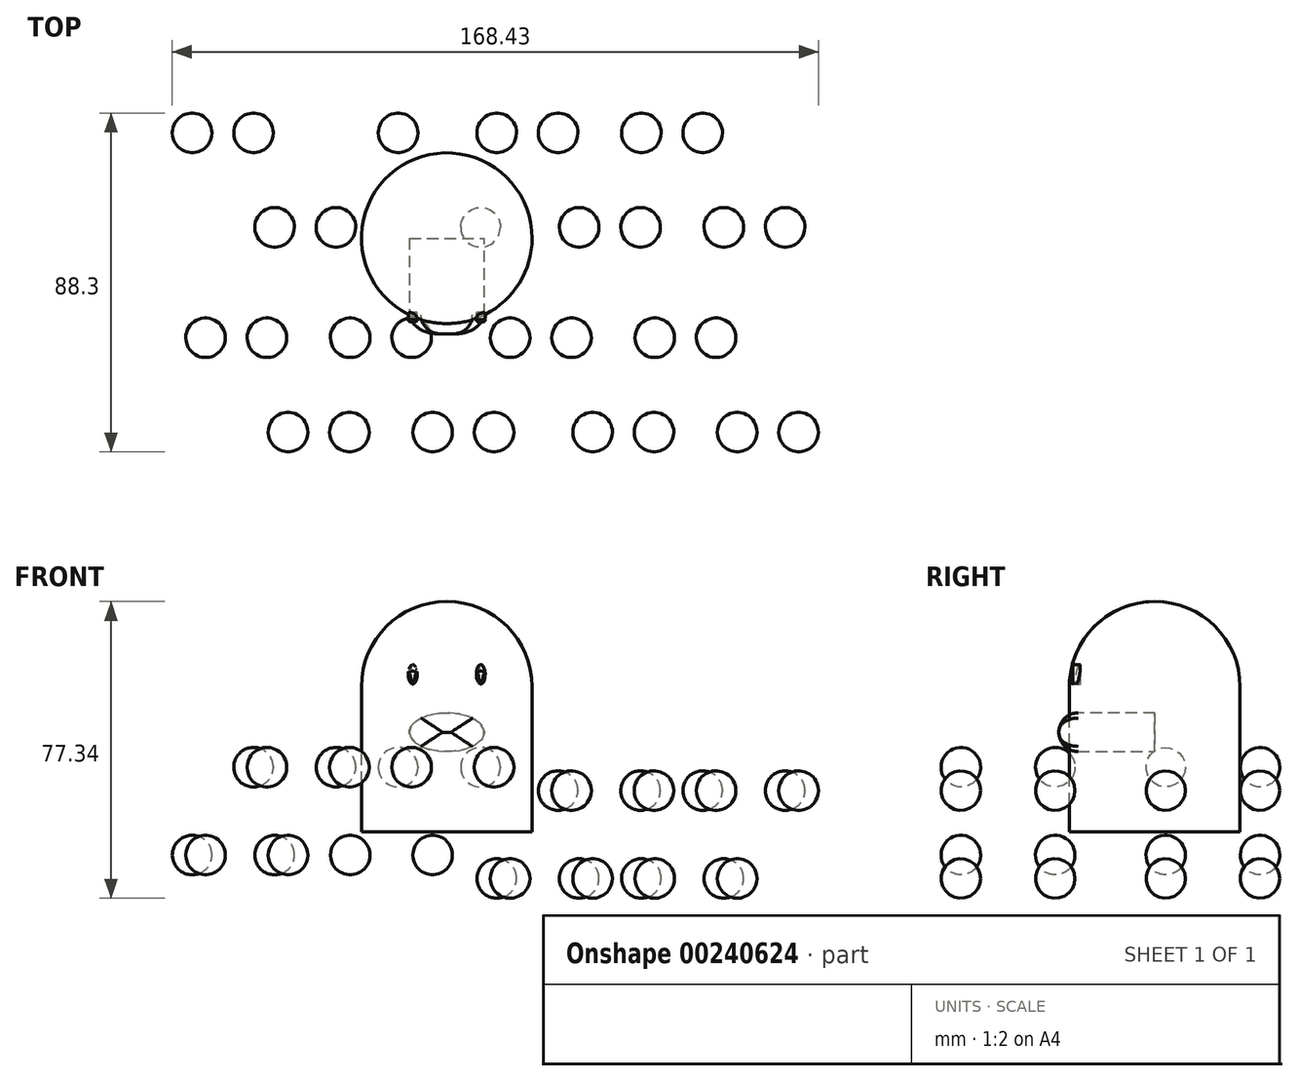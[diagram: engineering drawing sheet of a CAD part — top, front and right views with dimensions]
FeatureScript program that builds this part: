
annotation { "Feature Type Name" : "Feature", "Feature Type Description" : "" }
export const myFeature = defineFeature(function(context is Context, id is Id, definition is map)
    precondition{}
    {
        {
            var Q0;
            Q0=qCreatedBy(makeId("Right.planeOp"),FACE);
            var sketch = newSketch(context, id + "F0", { "sketchPlane" : qUnion([Q0])});
            skArc(sketch, "E0", {"start": v(22.25, 0) * mm, "mid": v(0, 22.25) * mm, "end": v(-22.25, 0) * mm});
            skLineSegment(sketch, "E1", {"start": v(22.25, 0) * mm, "end": v(-22.25, 0) * mm, "construction": true});
            skLineSegment(sketch, "E2.top", {"start": v(22.25, -37.74) * mm, "end": v(-22.25, -37.74) * mm});
            skLineSegment(sketch, "E2.left", {"start": v(22.25, 0) * mm, "end": v(22.25, -37.74) * mm});
            skLineSegment(sketch, "E2.right", {"start": v(-22.25, 0) * mm, "end": v(-22.25, -37.74) * mm});
            skLineSegment(sketch, "E3", {"start": v(0, 22.25) * mm, "end": v(0, -37.74) * mm});
            skSolve(sketch);
        }
        {
            var Q0;
            {var subQ0=sQuery(id+"F0.wireOp",EDGE,"E2.right");Q0=makeQuery(id+"F0.imprint","IMPRINT",FACE,{"disambiguationData":[TD([[makeQuery(id+"F0.imprint","IMPRINT",EDGE,{"derivedFrom":subQ0}),1.0]])]});}
            var Q1;
            Q1=sQuery(id+"F0.wireOp",EDGE,"E3");
            revolve(context, id + "F1", {"entities" : qUnion([Q0]), "axis" : qUnion([Q1]), "revolveType" : RevolveType.FULL});
        }
        {
            var Q0;
            Q0=qCreatedBy(makeId("Front.planeOp"),FACE);
            cPlane(context, id + "F2", {"entities" : qUnion([Q0]), "cplaneType" : CPlaneType.OFFSET, "offset" : 25 * mm, "width" : 150 * mm, "height" : 150 * mm});
        }
        {
            var Q0;
            Q0=qCreatedBy(id+"F2.planeOp",FACE);
            var sketch = newSketch(context, id + "F3", { "sketchPlane" : qUnion([Q0])});
            skLineSegment(sketch, "E4", {"start": v(0, 0) * mm, "end": v(0, 49.01) * mm, "construction": true});
            skEllipse(sketch, "E5", {"center": v(8.87, 3.27) * mm, "majorRadius": 2.53 * mm, "minorRadius": 1.14 * mm, "majorAxis": v(0, -1)});
            skEllipse(sketch, "E6", {"center": v(0, -11.83) * mm, "majorRadius": 9.76 * mm, "minorRadius": 5.04 * mm, "majorAxis": v(-1, 0)});
            skEllipse(sketch, "E7.MirrorC", {"center": v(-8.87, 3.27) * mm, "majorRadius": 2.53 * mm, "minorRadius": 1.14 * mm, "majorAxis": v(0, -1)});
            skSolve(sketch);
        }
        {
            var Q0;
            Q0=makeQuery(id+"F3.imprint","IMPRINT",FACE,{"disambiguationData":[TD([[makeQuery(id+"F3.imprint","IMPRINT",EDGE,{"derivedFrom":sQuery(id+"F3.wireOp",EDGE,"E5")}),1.0]])]});
            var Q1;
            Q1=makeQuery(id+"F3.imprint","IMPRINT",FACE,{"disambiguationData":[TD([[makeQuery(id+"F3.imprint","IMPRINT",EDGE,{"derivedFrom":sQuery(id+"F3.wireOp",EDGE,"E7.MirrorC")}),1.0]])]});
            var Q2;
            Q2=makeQuery(id+"F1.opRevolve","SWEPT_FACE",FACE,{"disambiguationData":[OSD([sQuery(id+"F0.wireOp",EDGE,"E0")])]});
            extrude(context, id + "F4", {"entities" : qUnion([Q0, Q1]), "operationType" : NewBodyOperationType.REMOVE, "oppositeDirection" : true, "endBoundEntityFace" : qUnion([Q2]), "depth" : 5.7 * mm});
        }
        {
            var Q0;
            Q0=makeQuery(id+"F4.boolean.opBoolean","COPY",FACE,{"derivedFrom":makeQuery(id+"F4.opExtrude","CAP_FACE",FACE,{"disambiguationData":[OSD([sQuery(id+"F3.wireOp",EDGE,"E5")])],"isStart":false})});
            var Q1;
            Q1=makeQuery(id+"F4.boolean.opBoolean","COPY",FACE,{"derivedFrom":makeQuery(id+"F4.opExtrude","CAP_FACE",FACE,{"disambiguationData":[OSD([sQuery(id+"F3.wireOp",EDGE,"E7.MirrorC")])],"isStart":false})});
            extrude(context, id + "F5", {"entities" : qUnion([Q0, Q1]), "depth" : 2 * mm});
        }
        {
            var Q0;
            Q0=makeQuery(id+"F5.opExtrude","CAP_FACE",FACE,{"disambiguationData":[OSD([sQuery(id+"F3.wireOp",EDGE,"E5")])],"isStart":false});
            var sketch = newSketch(context, id + "F6", { "sketchPlane" : qUnion([Q0])});
            skEllipse(sketch, "E8.0.0", {"center": v(8.87, 3.27) * mm, "majorRadius": 2.53 * mm, "minorRadius": 1.14 * mm, "majorAxis": v(0, -1)});
            skEllipse(sketch, "E9.0.0", {"center": v(-8.87, 3.27) * mm, "majorRadius": 2.53 * mm, "minorRadius": 1.14 * mm, "majorAxis": v(0, -1)});
            skArc(sketch, "E10", {"start": v(10, 3.27) * mm, "mid": v(8.87, 4.1) * mm, "end": v(7.72, 3.27) * mm});
            skArc(sketch, "E11", {"start": v(-7.72, 3.27) * mm, "mid": v(-8.87, 4.1) * mm, "end": v(-10, 3.27) * mm});
            skSolve(sketch);
        }
        {
            var Q0;
            {var subQ0=sQuery(id+"F6.wireOp",EDGE,"E10");Q0=makeQuery(id+"F6.imprint","IMPRINT",FACE,{"disambiguationData":[TD([[makeQuery(id+"F6.imprint","IMPRINT",EDGE,{"derivedFrom":subQ0}),1.0]])]});}
            var Q1;
            {var subQ0=sQuery(id+"F6.wireOp",EDGE,"E11");Q1=makeQuery(id+"F6.imprint","IMPRINT",FACE,{"disambiguationData":[TD([[makeQuery(id+"F6.imprint","IMPRINT",EDGE,{"derivedFrom":subQ0}),1.0]])]});}
            extrude(context, id + "F7", {"entities" : qUnion([Q0, Q1]), "depth" : .5 * mm});
        }
        {
            var Q0;
            Q0=makeQuery(id+"F3.imprint","IMPRINT",FACE,{"disambiguationData":[TD([[makeQuery(id+"F3.imprint","IMPRINT",EDGE,{"derivedFrom":sQuery(id+"F3.wireOp",EDGE,"E6")}),1.0]])]});
            extrude(context, id + "F8", {"entities" : qUnion([Q0]), "oppositeDirection" : true, "depth" : 25 * mm});
        }
        {
            var Q0;
            Q0=makeQuery(id+"F8.opExtrude","CAP_EDGE",EDGE,{"disambiguationData":[OSD([sQuery(id+"F3.wireOp",EDGE,"E6")])],"isStart":true});
            fillet(context, id + "F9", {"entities" : qUnion([Q0]), "radius" : 5 * mm, "tangentPropagation" : true, "allowEdgeOverflow" : false});
        }
        {
            var Q0;
            Q0=makeQuery(id+"F5.opExtrude","CAP_EDGE",EDGE,{"disambiguationData":[OSD([sQuery(id+"F3.wireOp",EDGE,"E7.MirrorC")])],"isStart":false});
            var Q1;
            Q1=makeQuery(id+"F7.opExtrude","CAP_EDGE",EDGE,{"disambiguationData":[OSD([sQuery(id+"F6.wireOp",EDGE,"E9.0.0")])],"isStart":false});
            var Q2;
            Q2=makeQuery(id+"F7.opExtrude","CAP_EDGE",EDGE,{"disambiguationData":[OSD([sQuery(id+"F6.wireOp",EDGE,"E11")])],"isStart":false});
            var Q3;
            Q3=makeQuery(id+"F7.opExtrude","CAP_EDGE",EDGE,{"disambiguationData":[OSD([sQuery(id+"F6.wireOp",EDGE,"E10")])],"isStart":false});
            var Q4;
            Q4=makeQuery(id+"F7.opExtrude","CAP_EDGE",EDGE,{"disambiguationData":[OSD([sQuery(id+"F6.wireOp",EDGE,"E8.0.0")])],"isStart":false});
            var Q5;
            Q5=makeQuery(id+"F5.opExtrude","CAP_EDGE",EDGE,{"disambiguationData":[OSD([sQuery(id+"F3.wireOp",EDGE,"E5")])],"isStart":false});
            fillet(context, id + "F10", {"entities" : qUnion([Q0, Q1, Q2, Q3, Q4, Q5]), "radius" : .5 * mm, "tangentPropagation" : true, "allowEdgeOverflow" : false});
        }
        {
            var Q0;
            Q0=makeQuery(id+"F1.opRevolve","SWEPT_FACE",FACE,{"disambiguationData":[OSD([sQuery(id+"F0.wireOp",EDGE,"E2.top")])]});
            var sketch = newSketch(context, id + "F11", { "sketchPlane" : qUnion([Q0])});
            skEllipse(sketch, "E12", {"center": v(24.82, -2.86) * mm, "majorRadius": 5.16 * mm, "minorRadius": 5.15 * mm, "majorAxis": v(1, 0)});
            skLineSegment(sketch, "E13", {"start": v(29.99, -2.86) * mm, "end": v(19.66, -2.86) * mm});
            skSolve(sketch);
        }
        {
            var Q0;
            {var subQ0=sQuery(id+"F11.wireOp",EDGE,"E13");var subQ1=sQuery(id+"F11.wireOp",EDGE,"E12");var subQ2=makeQuery(id+"F11.imprint","INTERSECT",VERTEX,{"disambiguationData":[OD(0.0)],"derivedFrom":[subQ1,subQ0]});Q0=makeQuery(id+"F11.imprint","IMPRINT",FACE,{"disambiguationData":[TD([[makeQuery(id+"F11.imprint","IMPRINT",EDGE,{"disambiguationData":[TD([[subQ2,1.0]])],"derivedFrom":subQ1}),1.0]])]});}
            var Q1;
            {var subQ0=sQuery(id+"F11.wireOp",EDGE,"E13");var subQ1=sQuery(id+"F11.wireOp",EDGE,"E12");var subQ2=makeQuery(id+"F11.imprint","INTERSECT",VERTEX,{"disambiguationData":[OD(1.0)],"derivedFrom":[subQ1,subQ0]});Q1=makeQuery(id+"F11.imprint","IMPRINT",FACE,{"disambiguationData":[TD([[makeQuery(id+"F11.imprint","IMPRINT",EDGE,{"disambiguationData":[TD([[subQ2,-1.0]])],"derivedFrom":subQ1}),1.0]])]});}
            var Q2;
            Q2=sQuery(id+"F11.wireOp",EDGE,"E13");
            revolve(context, id + "F12", {"entities" : qUnion([Q0, Q1]), "axis" : qUnion([Q2]), "revolveType" : RevolveType.FULL});
        }
        {
            var Q0;
            Q0=makeQuery(id+"F12.opRevolve","SWEPT_BODY",BODY,{"disambiguationData":[OSD([sQuery(id+"F11.wireOp",EDGE,"E12"),sQuery(id+"F11.wireOp",EDGE,"E13")])]});
            transform(context, id + "F13", {"entities" : qUnion([Q0]), "transformType" : TransformType.TRANSLATION_3D, "dx" : -53.7 * mm, "dy" : 0 * mm, "dz" : -3.8 * mm, "makeCopy" : true});
        }
        {
            var Q0;
            Q0=makeQuery(id+"F12.opRevolve","SWEPT_BODY",BODY,{"disambiguationData":[OSD([sQuery(id+"F11.wireOp",EDGE,"E12"),sQuery(id+"F11.wireOp",EDGE,"E13")])]});
            transform(context, id + "F14", {"entities" : qUnion([Q0]), "transformType" : TransformType.TRANSLATION_3D, "dx" : 25.7 * mm, "dy" : 0 * mm, "dz" : -9.9 * mm, "makeCopy" : false});
        }
        {
            var Q0;
            Q0=makeQuery(id+"F13.opPattern","COPY",BODY,{"derivedFrom":makeQuery(id+"F12.opRevolve","SWEPT_BODY",BODY,{"disambiguationData":[OSD([sQuery(id+"F11.wireOp",EDGE,"E12"),sQuery(id+"F11.wireOp",EDGE,"E13")])]}),"instanceName":"1"});
            var Q1;
            Q1=makeQuery(id+"F12.opRevolve","SWEPT_BODY",BODY,{"disambiguationData":[OSD([sQuery(id+"F11.wireOp",EDGE,"E12"),sQuery(id+"F11.wireOp",EDGE,"E13")])]});
            transform(context, id + "F15", {"entities" : qUnion([Q0, Q1]), "transformType" : TransformType.TRANSLATION_3D, "dx" : -21.5 * mm, "dy" : 24.6 * mm, "dz" : 0 * mm, "makeCopy" : true});
        }
        {
            var Q0;
            Q0=makeQuery(id+"F13.opPattern","COPY",BODY,{"derivedFrom":makeQuery(id+"F12.opRevolve","SWEPT_BODY",BODY,{"disambiguationData":[OSD([sQuery(id+"F11.wireOp",EDGE,"E12"),sQuery(id+"F11.wireOp",EDGE,"E13")])]}),"instanceName":"1"});
            var Q1;
            Q1=makeQuery(id+"F15.opPattern","COPY",BODY,{"derivedFrom":makeQuery(id+"F13.opPattern","COPY",BODY,{"derivedFrom":makeQuery(id+"F12.opRevolve","SWEPT_BODY",BODY,{"disambiguationData":[OSD([sQuery(id+"F11.wireOp",EDGE,"E12"),sQuery(id+"F11.wireOp",EDGE,"E13")])]}),"instanceName":"1"}),"instanceName":"1"});
            var Q2;
            Q2=makeQuery(id+"F15.opPattern","COPY",BODY,{"derivedFrom":makeQuery(id+"F12.opRevolve","SWEPT_BODY",BODY,{"disambiguationData":[OSD([sQuery(id+"F11.wireOp",EDGE,"E12"),sQuery(id+"F11.wireOp",EDGE,"E13")])]}),"instanceName":"1"});
            var Q3;
            Q3=makeQuery(id+"F12.opRevolve","SWEPT_BODY",BODY,{"disambiguationData":[OSD([sQuery(id+"F11.wireOp",EDGE,"E12"),sQuery(id+"F11.wireOp",EDGE,"E13")])]});
            transform(context, id + "F16", {"entities" : qUnion([Q0, Q1, Q2, Q3]), "transformType" : TransformType.TRANSLATION_3D, "dx" : 3.5 * mm, "dy" : -53.4 * mm, "dz" : 0 * mm, "makeCopy" : true});
        }
        {
            var Q0;
            Q0=makeQuery(id+"F12.opRevolve","SWEPT_BODY",BODY,{"disambiguationData":[OSD([sQuery(id+"F11.wireOp",EDGE,"E12"),sQuery(id+"F11.wireOp",EDGE,"E13")])]});
            var Q1;
            Q1=makeQuery(id+"F16.opPattern","COPY",BODY,{"derivedFrom":makeQuery(id+"F15.opPattern","COPY",BODY,{"derivedFrom":makeQuery(id+"F12.opRevolve","SWEPT_BODY",BODY,{"disambiguationData":[OSD([sQuery(id+"F11.wireOp",EDGE,"E12"),sQuery(id+"F11.wireOp",EDGE,"E13")])]}),"instanceName":"1"}),"instanceName":"1"});
            var Q2;
            Q2=makeQuery(id+"F16.opPattern","COPY",BODY,{"derivedFrom":makeQuery(id+"F12.opRevolve","SWEPT_BODY",BODY,{"disambiguationData":[OSD([sQuery(id+"F11.wireOp",EDGE,"E12"),sQuery(id+"F11.wireOp",EDGE,"E13")])]}),"instanceName":"1"});
            var Q3;
            Q3=makeQuery(id+"F15.opPattern","COPY",BODY,{"derivedFrom":makeQuery(id+"F12.opRevolve","SWEPT_BODY",BODY,{"disambiguationData":[OSD([sQuery(id+"F11.wireOp",EDGE,"E12"),sQuery(id+"F11.wireOp",EDGE,"E13")])]}),"instanceName":"1"});
            var Q4;
            Q4=makeQuery(id+"F16.opPattern","COPY",BODY,{"derivedFrom":makeQuery(id+"F13.opPattern","COPY",BODY,{"derivedFrom":makeQuery(id+"F12.opRevolve","SWEPT_BODY",BODY,{"disambiguationData":[OSD([sQuery(id+"F11.wireOp",EDGE,"E12"),sQuery(id+"F11.wireOp",EDGE,"E13")])]}),"instanceName":"1"}),"instanceName":"1"});
            var Q5;
            Q5=makeQuery(id+"F13.opPattern","COPY",BODY,{"derivedFrom":makeQuery(id+"F12.opRevolve","SWEPT_BODY",BODY,{"disambiguationData":[OSD([sQuery(id+"F11.wireOp",EDGE,"E12"),sQuery(id+"F11.wireOp",EDGE,"E13")])]}),"instanceName":"1"});
            var Q6;
            Q6=makeQuery(id+"F15.opPattern","COPY",BODY,{"derivedFrom":makeQuery(id+"F13.opPattern","COPY",BODY,{"derivedFrom":makeQuery(id+"F12.opRevolve","SWEPT_BODY",BODY,{"disambiguationData":[OSD([sQuery(id+"F11.wireOp",EDGE,"E12"),sQuery(id+"F11.wireOp",EDGE,"E13")])]}),"instanceName":"1"}),"instanceName":"1"});
            var Q7;
            Q7=makeQuery(id+"F16.opPattern","COPY",BODY,{"derivedFrom":makeQuery(id+"F15.opPattern","COPY",BODY,{"derivedFrom":makeQuery(id+"F13.opPattern","COPY",BODY,{"derivedFrom":makeQuery(id+"F12.opRevolve","SWEPT_BODY",BODY,{"disambiguationData":[OSD([sQuery(id+"F11.wireOp",EDGE,"E12"),sQuery(id+"F11.wireOp",EDGE,"E13")])]}),"instanceName":"1"}),"instanceName":"1"}),"instanceName":"1"});
            transform(context, id + "F17", {"entities" : qUnion([Q0, Q1, Q2, Q3, Q4, Q5, Q6, Q7]), "transformType" : TransformType.TRANSLATION_3D, "dx" : 37.7 * mm, "dy" : 0 * mm, "dz" : 0 * mm, "makeCopy" : true});
        }
        {
            var Q0;
            Q0=makeQuery(id+"F12.opRevolve","SWEPT_BODY",BODY,{"disambiguationData":[OSD([sQuery(id+"F11.wireOp",EDGE,"E12"),sQuery(id+"F11.wireOp",EDGE,"E13")])]});
            var Q1;
            Q1=makeQuery(id+"F15.opPattern","COPY",BODY,{"derivedFrom":makeQuery(id+"F12.opRevolve","SWEPT_BODY",BODY,{"disambiguationData":[OSD([sQuery(id+"F11.wireOp",EDGE,"E12"),sQuery(id+"F11.wireOp",EDGE,"E13")])]}),"instanceName":"1"});
            var Q2;
            Q2=makeQuery(id+"F17.opPattern","COPY",BODY,{"derivedFrom":makeQuery(id+"F16.opPattern","COPY",BODY,{"derivedFrom":makeQuery(id+"F15.opPattern","COPY",BODY,{"derivedFrom":makeQuery(id+"F12.opRevolve","SWEPT_BODY",BODY,{"disambiguationData":[OSD([sQuery(id+"F11.wireOp",EDGE,"E12"),sQuery(id+"F11.wireOp",EDGE,"E13")])]}),"instanceName":"1"}),"instanceName":"1"}),"instanceName":"1"});
            var Q3;
            Q3=makeQuery(id+"F17.opPattern","COPY",BODY,{"derivedFrom":makeQuery(id+"F16.opPattern","COPY",BODY,{"derivedFrom":makeQuery(id+"F12.opRevolve","SWEPT_BODY",BODY,{"disambiguationData":[OSD([sQuery(id+"F11.wireOp",EDGE,"E12"),sQuery(id+"F11.wireOp",EDGE,"E13")])]}),"instanceName":"1"}),"instanceName":"1"});
            var Q4;
            Q4=makeQuery(id+"F17.opPattern","COPY",BODY,{"derivedFrom":makeQuery(id+"F15.opPattern","COPY",BODY,{"derivedFrom":makeQuery(id+"F12.opRevolve","SWEPT_BODY",BODY,{"disambiguationData":[OSD([sQuery(id+"F11.wireOp",EDGE,"E12"),sQuery(id+"F11.wireOp",EDGE,"E13")])]}),"instanceName":"1"}),"instanceName":"1"});
            var Q5;
            Q5=makeQuery(id+"F17.opPattern","COPY",BODY,{"derivedFrom":makeQuery(id+"F12.opRevolve","SWEPT_BODY",BODY,{"disambiguationData":[OSD([sQuery(id+"F11.wireOp",EDGE,"E12"),sQuery(id+"F11.wireOp",EDGE,"E13")])]}),"instanceName":"1"});
            var Q6;
            Q6=makeQuery(id+"F16.opPattern","COPY",BODY,{"derivedFrom":makeQuery(id+"F15.opPattern","COPY",BODY,{"derivedFrom":makeQuery(id+"F12.opRevolve","SWEPT_BODY",BODY,{"disambiguationData":[OSD([sQuery(id+"F11.wireOp",EDGE,"E12"),sQuery(id+"F11.wireOp",EDGE,"E13")])]}),"instanceName":"1"}),"instanceName":"1"});
            var Q7;
            Q7=makeQuery(id+"F16.opPattern","COPY",BODY,{"derivedFrom":makeQuery(id+"F13.opPattern","COPY",BODY,{"derivedFrom":makeQuery(id+"F12.opRevolve","SWEPT_BODY",BODY,{"disambiguationData":[OSD([sQuery(id+"F11.wireOp",EDGE,"E12"),sQuery(id+"F11.wireOp",EDGE,"E13")])]}),"instanceName":"1"}),"instanceName":"1"});
            var Q8;
            Q8=makeQuery(id+"F16.opPattern","COPY",BODY,{"derivedFrom":makeQuery(id+"F12.opRevolve","SWEPT_BODY",BODY,{"disambiguationData":[OSD([sQuery(id+"F11.wireOp",EDGE,"E12"),sQuery(id+"F11.wireOp",EDGE,"E13")])]}),"instanceName":"1"});
            var Q9;
            Q9=makeQuery(id+"F17.opPattern","COPY",BODY,{"derivedFrom":makeQuery(id+"F16.opPattern","COPY",BODY,{"derivedFrom":makeQuery(id+"F13.opPattern","COPY",BODY,{"derivedFrom":makeQuery(id+"F12.opRevolve","SWEPT_BODY",BODY,{"disambiguationData":[OSD([sQuery(id+"F11.wireOp",EDGE,"E12"),sQuery(id+"F11.wireOp",EDGE,"E13")])]}),"instanceName":"1"}),"instanceName":"1"}),"instanceName":"1"});
            var Q10;
            Q10=makeQuery(id+"F17.opPattern","COPY",BODY,{"derivedFrom":makeQuery(id+"F16.opPattern","COPY",BODY,{"derivedFrom":makeQuery(id+"F15.opPattern","COPY",BODY,{"derivedFrom":makeQuery(id+"F13.opPattern","COPY",BODY,{"derivedFrom":makeQuery(id+"F12.opRevolve","SWEPT_BODY",BODY,{"disambiguationData":[OSD([sQuery(id+"F11.wireOp",EDGE,"E12"),sQuery(id+"F11.wireOp",EDGE,"E13")])]}),"instanceName":"1"}),"instanceName":"1"}),"instanceName":"1"}),"instanceName":"1"});
            var Q11;
            Q11=makeQuery(id+"F13.opPattern","COPY",BODY,{"derivedFrom":makeQuery(id+"F12.opRevolve","SWEPT_BODY",BODY,{"disambiguationData":[OSD([sQuery(id+"F11.wireOp",EDGE,"E12"),sQuery(id+"F11.wireOp",EDGE,"E13")])]}),"instanceName":"1"});
            var Q12;
            Q12=makeQuery(id+"F15.opPattern","COPY",BODY,{"derivedFrom":makeQuery(id+"F13.opPattern","COPY",BODY,{"derivedFrom":makeQuery(id+"F12.opRevolve","SWEPT_BODY",BODY,{"disambiguationData":[OSD([sQuery(id+"F11.wireOp",EDGE,"E12"),sQuery(id+"F11.wireOp",EDGE,"E13")])]}),"instanceName":"1"}),"instanceName":"1"});
            var Q13;
            Q13=makeQuery(id+"F16.opPattern","COPY",BODY,{"derivedFrom":makeQuery(id+"F15.opPattern","COPY",BODY,{"derivedFrom":makeQuery(id+"F13.opPattern","COPY",BODY,{"derivedFrom":makeQuery(id+"F12.opRevolve","SWEPT_BODY",BODY,{"disambiguationData":[OSD([sQuery(id+"F11.wireOp",EDGE,"E12"),sQuery(id+"F11.wireOp",EDGE,"E13")])]}),"instanceName":"1"}),"instanceName":"1"}),"instanceName":"1"});
            transform(context, id + "F18", {"entities" : qUnion([Q0, Q1, Q2, Q3, Q4, Q5, Q6, Q7, Q8, Q9, Q10, Q11, Q12, Q13]), "transformType" : TransformType.TRANSLATION_3D, "dx" : -16 * mm, "dy" : 0 * mm, "dz" : -22.9 * mm, "makeCopy" : true});
        }
        {
            var Q0;
            Q0=makeQuery(id+"F1.opRevolve","SWEPT_BODY",BODY,{"disambiguationData":[OSD([sQuery(id+"F0.wireOp",EDGE,"E0"),sQuery(id+"F0.wireOp",EDGE,"E2.top"),sQuery(id+"F0.wireOp",EDGE,"E2.right"),sQuery(id+"F0.wireOp",EDGE,"E3")])]});
            var Q1;
            Q1=makeQuery(id+"F5.opExtrude","SWEPT_BODY",BODY,{"disambiguationData":[OSD([sQuery(id+"F3.wireOp",EDGE,"E7.MirrorC")])]});
            var Q2;
            Q2=makeQuery(id+"F7.opExtrude","SWEPT_BODY",BODY,{"disambiguationData":[OSD([sQuery(id+"F6.wireOp",EDGE,"E9.0.0"),sQuery(id+"F6.wireOp",EDGE,"E11")])]});
            var Q3;
            Q3=makeQuery(id+"F8.opExtrude","SWEPT_BODY",BODY,{"disambiguationData":[OSD([sQuery(id+"F3.wireOp",EDGE,"E6")])]});
            var Q4;
            Q4=makeQuery(id+"F5.opExtrude","SWEPT_BODY",BODY,{"disambiguationData":[OSD([sQuery(id+"F3.wireOp",EDGE,"E5")])]});
            var Q5;
            Q5=makeQuery(id+"F7.opExtrude","SWEPT_BODY",BODY,{"disambiguationData":[OSD([sQuery(id+"F6.wireOp",EDGE,"E8.0.0"),sQuery(id+"F6.wireOp",EDGE,"E10")])]});
            transform(context, id + "F19", {"entities" : qUnion([Q0, Q1, Q2, Q3, Q4, Q5]), "transformType" : TransformType.TRANSLATION_3D, "dx" : 0 * mm, "dy" : 0 * mm, "dz" : -20.6 * mm, "makeCopy" : false});
        }
    });
